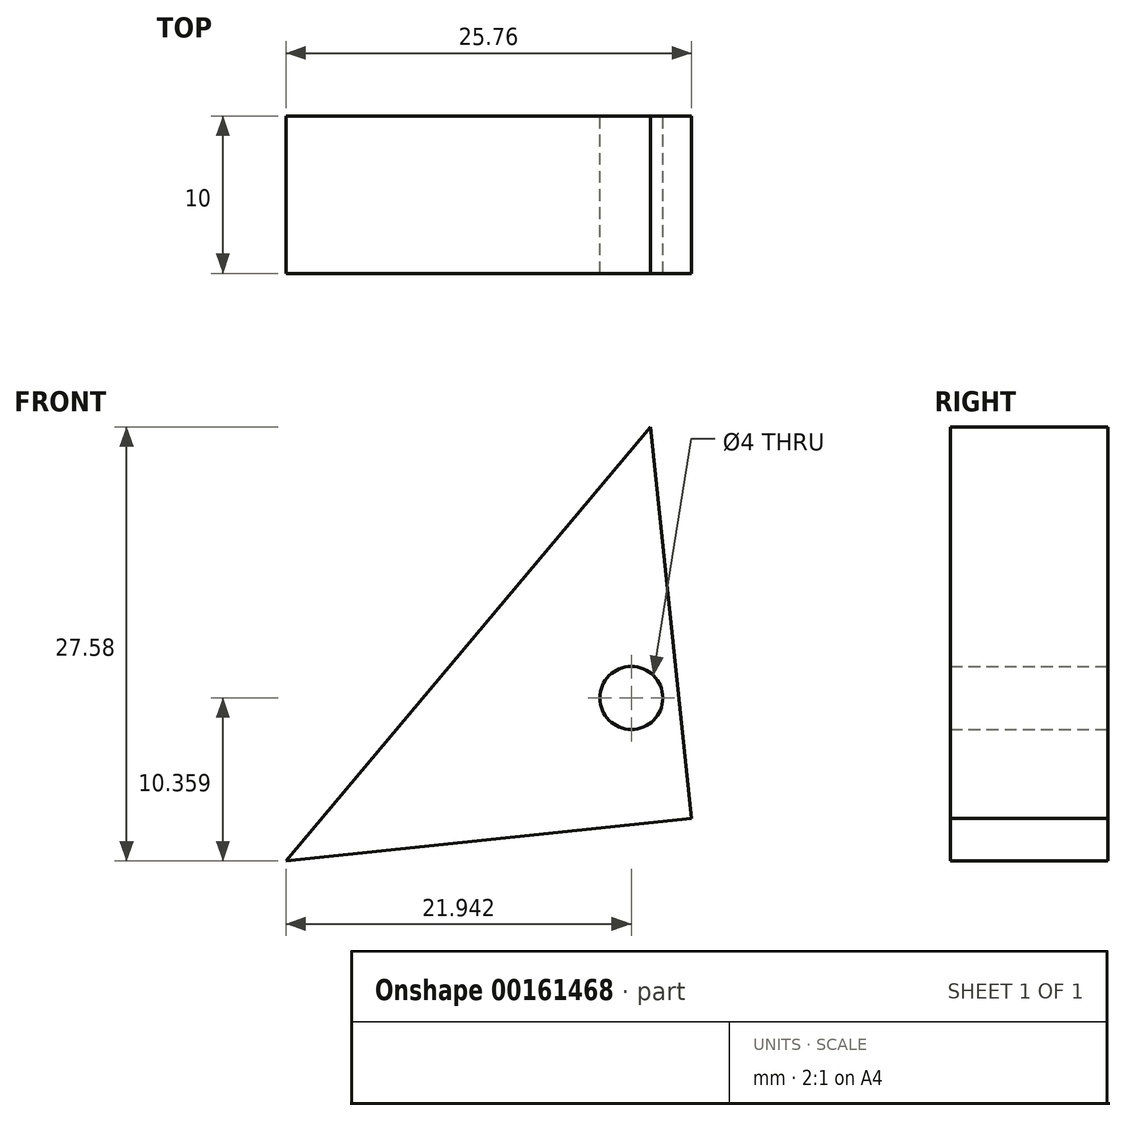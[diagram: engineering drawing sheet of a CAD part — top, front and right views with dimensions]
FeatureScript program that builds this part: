
annotation { "Feature Type Name" : "Feature", "Feature Type Description" : "" }
export const myFeature = defineFeature(function(context is Context, id is Id, definition is map)
    precondition{}
    {
        {
            var Q0;
            Q0=qCreatedBy(makeId("Front.planeOp"),FACE);
            var sketch = newSketch(context, id + "F0", { "sketchPlane" : qUnion([Q0])});
            skLineSegment(sketch, "E0", {"start": v(-24.32, 58.9) * mm, "end": v(-21.7, 34.05) * mm});
            skLineSegment(sketch, "E1", {"start": v(-21.7, 34.05) * mm, "end": v(-47.47, 31.33) * mm});
            skLineSegment(sketch, "E2", {"start": v(-47.47, 31.33) * mm, "end": v(-24.32, 58.9) * mm});
            skPoint(sketch, "E3", {"position": v(-25.53, 41.69) * mm});
            skSolve(sketch);
        }
        {
            var Q0;
            Q0=makeQuery(id+"F0.imprint","IMPRINT",FACE,{"disambiguationData":[TD([[makeQuery(id+"F0.imprint","IMPRINT",EDGE,{"derivedFrom":sQuery(id+"F0.wireOp",EDGE,"E0")}),-1.0]])]});
            extrude(context, id + "F1", {"entities" : qUnion([Q0]), "depth" : 10 * mm});
        }
        {
            var Q0;
            Q0=sQuery(id+"F0.wireOp",VERTEX,"E3");
            var Q1;
            Q1=makeQuery(id+"F1.opExtrude","SWEPT_BODY",BODY,{"disambiguationData":[OSD([sQuery(id+"F0.wireOp",EDGE,"E0"),sQuery(id+"F0.wireOp",EDGE,"E1"),sQuery(id+"F0.wireOp",EDGE,"E2")])]});
            hole(context, id + "F2", {"style" : HoleStyle.SIMPLE, "endStyle" : HoleEndStyle.BLIND, "oppositeDirection" : true, "holeDiameter" : 4 * mm, "holeDepth" : 12 * mm, "startFromSketch" : true, "locations" : qUnion([Q0]), "scope" : qUnion([Q1])});
        }
    });
